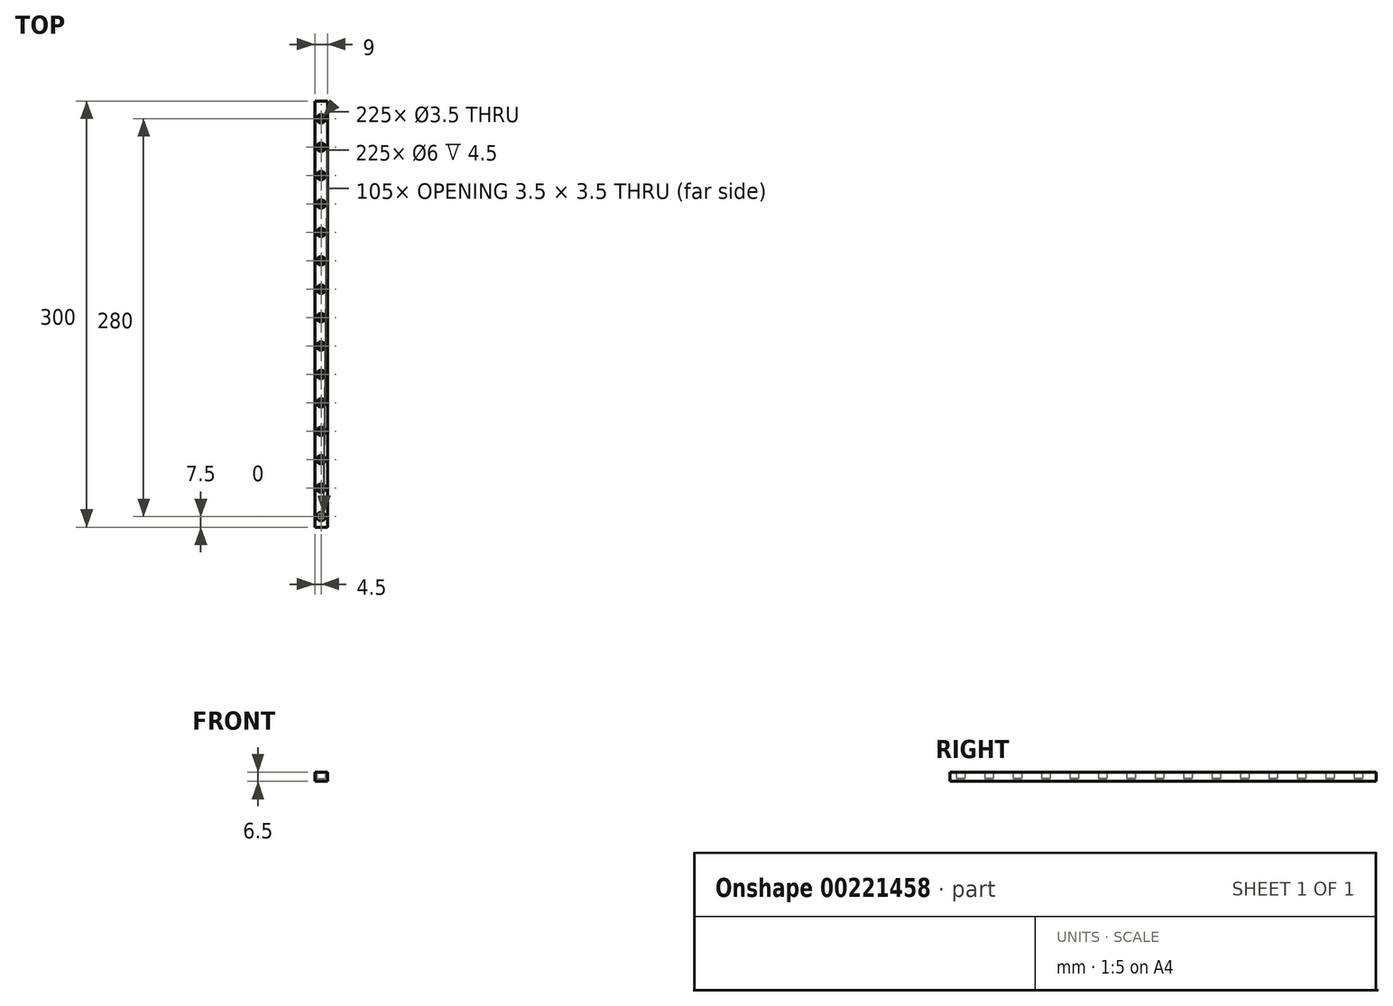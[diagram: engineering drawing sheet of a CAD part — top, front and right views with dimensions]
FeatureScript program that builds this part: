
annotation { "Feature Type Name" : "Feature", "Feature Type Description" : "" }
export const myFeature = defineFeature(function(context is Context, id is Id, definition is map)
    precondition{}
    {
        {
            var Q0;
            Q0=qCreatedBy(makeId("Front.planeOp"),FACE);
            var sketch = newSketch(context, id + "F0", { "sketchPlane" : qUnion([Q0])});
            skLineSegment(sketch, "E0.bottom", {"start": v(0, 0) * mm, "end": v(9, 0) * mm});
            skLineSegment(sketch, "E0.top", {"start": v(0, 6.5) * mm, "end": v(9, 6.5) * mm});
            skLineSegment(sketch, "E0.left", {"start": v(0, 0) * mm, "end": v(0, 6.5) * mm});
            skLineSegment(sketch, "E0.right", {"start": v(9, 0) * mm, "end": v(9, 6.5) * mm});
            skSolve(sketch);
        }
        {
            var Q0;
            Q0 = qSketchRegion(id + "F0", true);
            extrude(context, id + "F1", {"entities" : qUnion([Q0]), "depth" : 300 * mm});
        }
        {
            var Q0;
            Q0=makeQuery(id+"F1.opExtrude","SWEPT_FACE",FACE,{"disambiguationData":[OSD([sQuery(id+"F0.wireOp",EDGE,"E0.top")])]});
            var sketch = newSketch(context, id + "F2", { "sketchPlane" : qUnion([Q0])});
            skPoint(sketch, "E1", {"position": v(4.5, -292.5) * mm});
            skPoint(sketch, "E1.positionSnap0", {"position": v(4.5, -300) * mm});
            skPoint(sketch, "E2.0.1.0", {"position": v(4.5, -272.5) * mm});
            skPoint(sketch, "E2.0.2.0", {"position": v(4.5, -252.5) * mm});
            skPoint(sketch, "E2.0.3.0", {"position": v(4.5, -232.5) * mm});
            skPoint(sketch, "E2.0.4.0", {"position": v(4.5, -212.5) * mm});
            skPoint(sketch, "E2.0.5.0", {"position": v(4.5, -192.5) * mm});
            skPoint(sketch, "E2.0.6.0", {"position": v(4.5, -172.5) * mm});
            skPoint(sketch, "E2.0.7.0", {"position": v(4.5, -152.5) * mm});
            skPoint(sketch, "E2.0.8.0", {"position": v(4.5, -132.5) * mm});
            skPoint(sketch, "E2.0.9.0", {"position": v(4.5, -112.5) * mm});
            skPoint(sketch, "E2.0.10.0", {"position": v(4.5, -92.5) * mm});
            skPoint(sketch, "E2.0.11.0", {"position": v(4.5, -72.5) * mm});
            skPoint(sketch, "E2.0.12.0", {"position": v(4.5, -52.5) * mm});
            skLineSegment(sketch, "E2.direction1", {"start": v(4.5, -292.5) * mm, "end": v(29.5, -292.5) * mm, "construction": true});
            skLineSegment(sketch, "E2.direction2", {"start": v(4.5, -292.5) * mm, "end": v(4.5, -272.5) * mm, "construction": true});
            skPoint(sketch, "E3.0.0.13", {"position": v(4.5, -32.5) * mm});
            skPoint(sketch, "E4.0.0.14", {"position": v(4.5, -12.5) * mm});
            skSolve(sketch);
        }
        {
            var Q0;
            Q0=sQuery(id+"F2.wireOp",VERTEX,"E1");
            var Q1;
            Q1=sQuery(id+"F2.wireOp",VERTEX,"E2.0.1.0");
            var Q2;
            Q2=sQuery(id+"F2.wireOp",VERTEX,"E2.0.2.0");
            var Q3;
            Q3=sQuery(id+"F2.wireOp",VERTEX,"E2.0.3.0");
            var Q4;
            Q4=sQuery(id+"F2.wireOp",VERTEX,"E2.0.4.0");
            var Q5;
            Q5=sQuery(id+"F2.wireOp",VERTEX,"E2.0.5.0");
            var Q6;
            Q6=sQuery(id+"F2.wireOp",VERTEX,"E2.0.6.0");
            var Q7;
            Q7=sQuery(id+"F2.wireOp",VERTEX,"E2.0.7.0");
            var Q8;
            Q8=sQuery(id+"F2.wireOp",VERTEX,"E2.0.8.0");
            var Q9;
            Q9=sQuery(id+"F2.wireOp",VERTEX,"E2.0.9.0");
            var Q10;
            Q10=sQuery(id+"F2.wireOp",VERTEX,"E2.0.10.0");
            var Q11;
            Q11=sQuery(id+"F2.wireOp",VERTEX,"E2.0.11.0");
            var Q12;
            Q12=sQuery(id+"F2.wireOp",VERTEX,"E2.0.12.0");
            var Q13;
            Q13=sQuery(id+"F2.wireOp",VERTEX,"E3.0.0.13");
            var Q14;
            Q14=sQuery(id+"F2.wireOp",VERTEX,"E4.0.0.14");
            var Q15;
            Q15=makeQuery(id+"F1.opExtrude","SWEPT_BODY",BODY,{"disambiguationData":[OSD([sQuery(id+"F0.wireOp",EDGE,"E0.bottom"),sQuery(id+"F0.wireOp",EDGE,"E0.top"),sQuery(id+"F0.wireOp",EDGE,"E0.left"),sQuery(id+"F0.wireOp",EDGE,"E0.right")])]});
            hole(context, id + "F3", {"style" : HoleStyle.C_BORE, "endStyle" : HoleEndStyle.THROUGH, "holeDiameter" : 3.5 * mm, "cBoreDiameter" : 6 * mm, "cBoreDepth" : 4.5 * mm, "locations" : qUnion([Q0, Q1, Q2, Q3, Q4, Q5, Q6, Q7, Q8, Q9, Q10, Q11, Q12, Q13, Q14]), "scope" : qUnion([Q15]), "isTappedThrough" : true});
        }
    });
